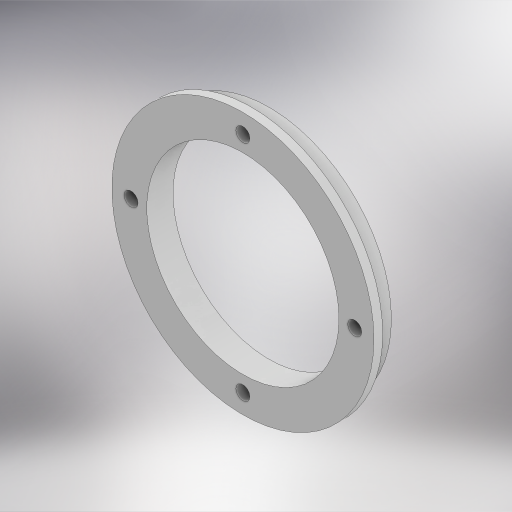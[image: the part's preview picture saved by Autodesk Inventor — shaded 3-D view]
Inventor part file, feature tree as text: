
AUTODESK INVENTOR PART (.ipt)
format: ipt  version: 2023.4 (Build 274418000, 418)  size: 349,184 bytes
history: native  units: in
note: dims shown in document units (in); Inventor stores cm internally (conversion verified against a paired STEP export)
features: sketch x4, extrude x2, hole x2
ambient origin geometry x8: Origin, YZ Plane, XZ Plane, XY Plane, X Axis, Y Axis, Z Axis, Center Point
bodies: Solid1 (feature_tree)
feature tree (8):
  extrude  "Extrusion1"  Depth=0.25in TaperAngle=0.0deg
  hole  "Hole1"  [1 undecoded]
  extrude  "Extrusion4"  Depth=0.25in
  hole  "Hole2"  [1 undecoded]
  sketch  "Sketch1"  dims[d0=3.5in d2=0.25in d3=0.0in]
  sketch  "Sketch3"  dims[d4=3.26in d5=45.0deg]
  sketch  "Sketch7"  dims[d6=1.5748in d8=360.0deg]
  sketch  "Sketch8"  dims[d10=0.156in d11=0.38in d12=0.375in d13=0.25in d14=0.5635in d15=1.0in d16=0.8108in d20=2.75in d25=3.75in d26=0.125in d27=0.0in d28=3.2in d29=0.201in d30=0.75in d31=0.375in d32=0.25in d33=0.5635in d34=0.16in d35=0.0in d36=1.5748in d38=360.0deg]
note: 2 required parameter values undecoded (feature->parameter linkage not recoverable at this tier; creation-order binding heuristic only, values carry confidence <= 0.55)
